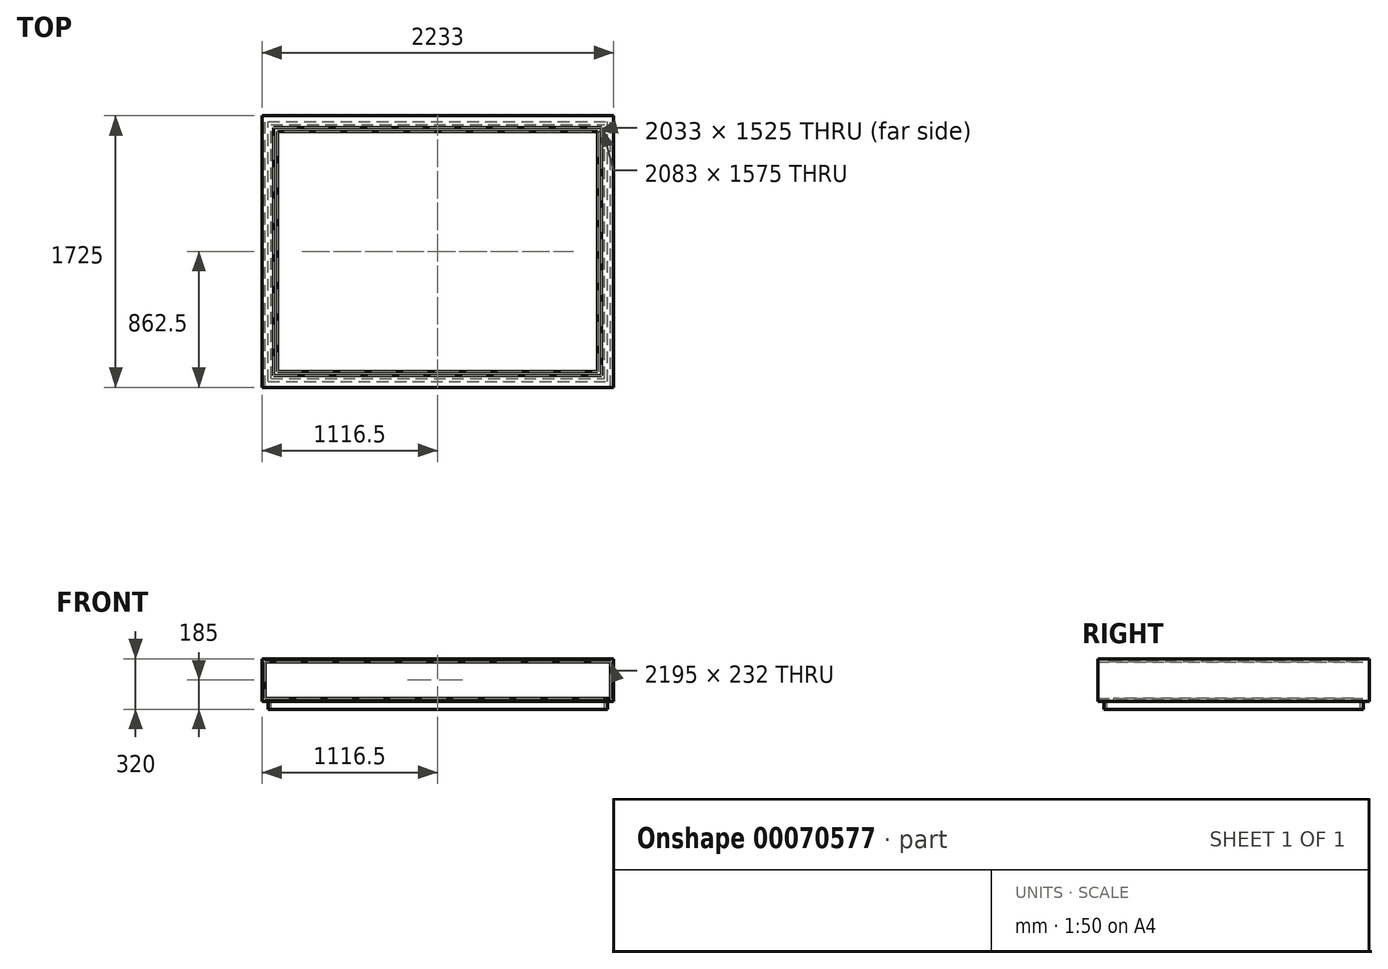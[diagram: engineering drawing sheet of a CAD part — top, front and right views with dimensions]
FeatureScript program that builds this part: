
annotation { "Feature Type Name" : "Feature", "Feature Type Description" : "" }
export const myFeature = defineFeature(function(context is Context, id is Id, definition is map)
    precondition{}
    {
        {
            var Q0;
            Q0=qCreatedBy(makeId("Front.planeOp"),FACE);
            var sketch = newSketch(context, id + "F0", { "sketchPlane" : qUnion([Q0])});
            skLineSegment(sketch, "E0.bottom", {"start": v(0, 0) * mm, "end": v(2233, 0) * mm});
            skLineSegment(sketch, "E0.top", {"start": v(0, 270) * mm, "end": v(2233, 270) * mm});
            skLineSegment(sketch, "E0.left", {"start": v(0, 0) * mm, "end": v(0, 270) * mm});
            skLineSegment(sketch, "E0.right", {"start": v(2233, 0) * mm, "end": v(2233, 270) * mm});
            skLineSegment(sketch, "E1.bottom", {"start": v(19, 251) * mm, "end": v(2214, 251) * mm});
            skLineSegment(sketch, "E1.top", {"start": v(19, 19) * mm, "end": v(2214, 19) * mm});
            skLineSegment(sketch, "E1.left", {"start": v(19, 251) * mm, "end": v(19, 19) * mm});
            skLineSegment(sketch, "E1.right", {"start": v(2214, 251) * mm, "end": v(2214, 19) * mm});
            skSolve(sketch);
        }
        {
            var Q0;
            Q0=makeQuery(id+"F0.imprint","IMPRINT",FACE,{"disambiguationData":[TD([[makeQuery(id+"F0.imprint","IMPRINT",EDGE,{"derivedFrom":sQuery(id+"F0.wireOp",EDGE,"E0.bottom")}),1.0]])]});
            extrude(context, id + "F1", {"entities" : qUnion([Q0]), "endBound" : BoundingType.SYMMETRIC, "depth" : 1725 * mm});
        }
        {
            var Q0;
            Q0=makeQuery(id+"F1.opExtrude","SWEPT_FACE",FACE,{"disambiguationData":[OSD([sQuery(id+"F0.wireOp",EDGE,"E0.top")])]});
            var sketch = newSketch(context, id + "F2", { "sketchPlane" : qUnion([Q0])});
            skLineSegment(sketch, "E2.bottom", {"start": v(75, 787.5) * mm, "end": v(2158, 787.5) * mm});
            skLineSegment(sketch, "E2.top", {"start": v(75, -787.5) * mm, "end": v(2158, -787.5) * mm});
            skLineSegment(sketch, "E2.left", {"start": v(75, 787.5) * mm, "end": v(75, -787.5) * mm});
            skLineSegment(sketch, "E2.right", {"start": v(2158, 787.5) * mm, "end": v(2158, -787.5) * mm});
            skSolve(sketch);
        }
        {
            var Q0;
            Q0=makeQuery(id+"F2.imprint","IMPRINT",FACE,{"disambiguationData":[TD([[makeQuery(id+"F2.imprint","IMPRINT",EDGE,{"derivedFrom":sQuery(id+"F2.wireOp",EDGE,"E2.bottom")}),-1.0]])]});
            extrude(context, id + "F3", {"entities" : qUnion([Q0]), "operationType" : NewBodyOperationType.REMOVE, "oppositeDirection" : true, "depth" : 38 * mm});
        }
        {
            var Q0;
            Q0=makeQuery(id+"F1.opExtrude","SWEPT_FACE",FACE,{"disambiguationData":[OSD([sQuery(id+"F0.wireOp",EDGE,"E0.bottom")])]});
            var sketch = newSketch(context, id + "F4", { "sketchPlane" : qUnion([Q0])});
            skLineSegment(sketch, "E3.bottom", {"start": v(38, 824.5) * mm, "end": v(2195, 824.5) * mm});
            skLineSegment(sketch, "E3.top", {"start": v(38, -824.5) * mm, "end": v(2195, -824.5) * mm});
            skLineSegment(sketch, "E3.left", {"start": v(38, 824.5) * mm, "end": v(38, -824.5) * mm});
            skLineSegment(sketch, "E3.right", {"start": v(2195, 824.5) * mm, "end": v(2195, -824.5) * mm});
            skLineSegment(sketch, "E4.bottom", {"start": v(57, 805.5) * mm, "end": v(2176, 805.5) * mm});
            skLineSegment(sketch, "E4.top", {"start": v(57, -805.5) * mm, "end": v(2176, -805.5) * mm});
            skLineSegment(sketch, "E4.left", {"start": v(57, 805.5) * mm, "end": v(57, -805.5) * mm});
            skLineSegment(sketch, "E4.right", {"start": v(2176, 805.5) * mm, "end": v(2176, -805.5) * mm});
            skSolve(sketch);
        }
        {
            var Q0;
            Q0=makeQuery(id+"F4.imprint","IMPRINT",FACE,{"disambiguationData":[TD([[makeQuery(id+"F4.imprint","IMPRINT",EDGE,{"derivedFrom":sQuery(id+"F4.wireOp",EDGE,"E3.bottom")}),-1.0]])]});
            extrude(context, id + "F5", {"entities" : qUnion([Q0]), "operationType" : NewBodyOperationType.ADD, "depth" : 50 * mm});
        }
        {
            var Q0;
            Q0=makeQuery(id+"F5.boolean.opBoolean","SPLIT",FACE,{"disambiguationData":[TD([makeQuery(id+"F5.opExtrude","SWEPT_FACE",FACE,{"disambiguationData":[OSD([sQuery(id+"F4.wireOp",EDGE,"E4.bottom")])]})])],"derivedFrom":makeQuery(id+"F1.opExtrude","SWEPT_FACE",FACE,{"disambiguationData":[OSD([sQuery(id+"F0.wireOp",EDGE,"E0.bottom")])]})});
            var sketch = newSketch(context, id + "F6", { "sketchPlane" : qUnion([Q0])});
            skLineSegment(sketch, "E5.bottom", {"start": v(100, 762.5) * mm, "end": v(2133, 762.5) * mm});
            skLineSegment(sketch, "E5.top", {"start": v(100, -762.5) * mm, "end": v(2133, -762.5) * mm});
            skLineSegment(sketch, "E5.left", {"start": v(100, 762.5) * mm, "end": v(100, -762.5) * mm});
            skLineSegment(sketch, "E5.right", {"start": v(2133, 762.5) * mm, "end": v(2133, -762.5) * mm});
            skSolve(sketch);
        }
        {
            var Q0;
            Q0=makeQuery(id+"F6.imprint","IMPRINT",FACE,{"disambiguationData":[TD([[makeQuery(id+"F6.imprint","IMPRINT",EDGE,{"derivedFrom":sQuery(id+"F6.wireOp",EDGE,"E5.bottom")}),-1.0]])]});
            extrude(context, id + "F7", {"entities" : qUnion([Q0]), "operationType" : NewBodyOperationType.REMOVE, "oppositeDirection" : true, "depth" : 25 * mm});
        }
    });
